# Revit family: ITK_Вставка для модулей Keystone Jack
name_source: partatom
category: Обобщенные модели
units: mm (PartAtom-declared; Revit-internal decimal feet)

## family parameters
Всегда вертикально = Да
Может служить основой для арматурных стержней = Нет
На основе рабочей плоскости = Нет
Общий = Нет
При загрузке вырезать с полостями = Нет
Размер круглого соединителя = Использовать диаметр
Тип детали = Нормальный
Точка расчета площади = Нет

## types (2) — shared parameters
ADSK_URL страницы изделия = https://www.itk-group.ru
ADSK_Версия Revit = 2019
ADSK_Версия семейства = 1.0
ADSK_Группирование = I. ЩИТЫ И ПУЛЬТЫ
ADSK_Единица измерения = шт
ADSK_Завод-изготовитель = IEK
ADSK_Материал наименование = Пластик
IEK_URL = https://www.itk-group.ru
IEK_Описание = Соответствие международным стандартам качества, что обеспечивает совместимость с компонентами для СКС и с кабелем других производителей.
Изготовлены из высококачественных негорючих материалов и отличаются надежностью и удобством эксплуатации.
KSI_CMa_Строительные материалы = 01.7.14.03
URL = https://www.iek.ru
Высота = 45 мм
Глубина = 22 мм
Изготовитель = ITK
Материал = Пластик белый
Степень защиты = IP20
zero-valued in all types: ADSK_Масса

## per-type parameters (varying)
| type | ADSK_Наименование | IEK_Цена за единицу | Ширина |
| CS6-11M | IITK Вставка 45х22,5мм для 1 мод. Keystone Jack с маркером | 52 | 23 мм |
| CS6-12M | ITK Вставка 45х45мм для 1 мод. Keystone Jack с маркером | 56.38 | 45 мм |

note: column(s) folded — value = type name in every type: ADSK_Код изделия
